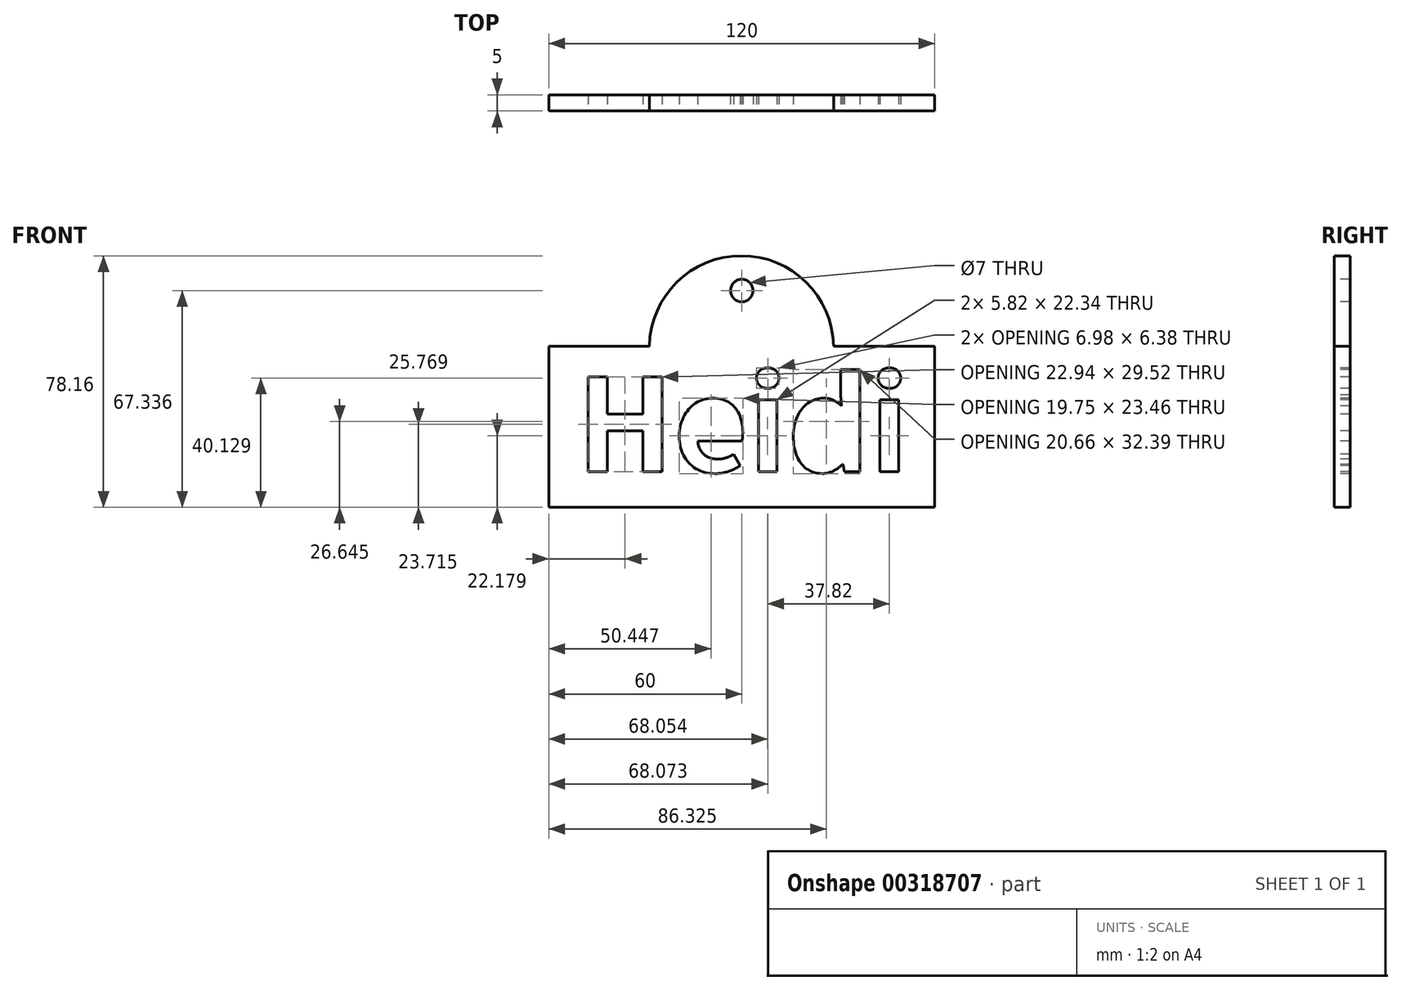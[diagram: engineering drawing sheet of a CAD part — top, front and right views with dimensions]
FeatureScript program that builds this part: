
annotation { "Feature Type Name" : "Feature", "Feature Type Description" : "" }
export const myFeature = defineFeature(function(context is Context, id is Id, definition is map)
    precondition{}
    {
        {
            var Q0;
            Q0=qCreatedBy(makeId("Front.planeOp"),FACE);
            var sketch = newSketch(context, id + "F0", { "sketchPlane" : qUnion([Q0])});
            skLineSegment(sketch, "E0.bottom", {"start": v(60, 25) * mm, "end": v(-60, 25) * mm});
            skLineSegment(sketch, "E0.top", {"start": v(60, -25) * mm, "end": v(-60, -25) * mm});
            skLineSegment(sketch, "E0.left", {"start": v(60, 25) * mm, "end": v(60, -25) * mm});
            skLineSegment(sketch, "E0.right", {"start": v(-60, 25) * mm, "end": v(-60, -25) * mm});
            skPoint(sketch, "E0.middle", {"position": v(0, 0) * mm});
            skArc(sketch, "E1", {"start": v(28.54, 25) * mm, "mid": v(-0.1, 53.16) * mm, "end": v(-28.72, 25) * mm});
            skCircle(sketch, "E2", {"center": v(0, 42.34) * mm, "radius": 3.5 * mm});
            skText(sketch, "E3", { "text": "Heidi\n", "fontName": "NotoSansCJKkr-Bold.otf"});
            const initialGuessF0  = {"E3": [-0.05138, -0.01399, 1, 0, 0.02872]};
            skSetInitialGuess(sketch, initialGuessF0);
            skSolve(sketch);
        }
        {
            var Q0;
            Q0=makeQuery(id+"F0.imprint","IMPRINT",FACE,{"disambiguationData":[TD([[makeQuery(id+"F0.imprint","IMPRINT",EDGE,{"derivedFrom":sQuery(id+"F0.wireOp",EDGE,"E0.top")}),-1.0]])]});
            var Q1;
            {var subQ0=sQuery(id+"F0.wireOp",EDGE,"E1");Q1=makeQuery(id+"F0.imprint","IMPRINT",FACE,{"disambiguationData":[TD([[makeQuery(id+"F0.imprint","IMPRINT",EDGE,{"derivedFrom":subQ0}),1.0]])]});}
            extrude(context, id + "F1", {"entities" : qUnion([Q0, Q1]), "oppositeDirection" : true, "depth" : 5 * mm});
        }
    });
